# Revit family: Emeco_1inch_Reclaimed_Chair
name_source: partatom
category: Furniture
revit_build: Autodesk Revit 2016 (Build: 20150714_1515(x64)
units: mm (PartAtom-declared; Revit-internal decimal feet)

## family parameters
Always vertical = Yes
Cut with Voids When Loaded = No
OmniClass Number = 23.40.20.00
OmniClass Title = General Furniture and Specialties
Room Calculation Point = No
Shared = No
Work Plane-Based = No

## types (8) — shared parameters
1" Reclaimed Chair = Bordeaux
Depth = 1' - 8 29/32"
Height = 2' - 7 3/32"
Manufacturer = Emeco
Model = 1inch Reclaimed Chair
URL = https://www.emeco.net
Width = 1' - 8 19/32"

## per-type parameters (varying)
| type | Chair | Chair Material | Weight |
| 1inch Reclaimed Chair - Blue | Sand | Emeco-Wood_Polypropylene - Dark Grey | 11.5lb |
| 1inch Reclaimed Chair - Sand | Sand | Emeco-Wood_Polypropylene - Sand | 11.5lb |
| 1inch Reclaimed Chair - Light Grey | Light Grey | Emeco-Wood_Polypropylene - Light Grey | 11.5lb |
| 1inch Reclaimed Chair - Green | Green | Emeco-Wood_Polypropylene - Green | 11.5lb |
| 1inch Reclaimed Chair - Bordeaux | Bordeaux | Emeco-Wood_Polypropylene - Bordeaux | 11.5lb |
| 1inch Reclaimed Chair - Brown | Brown | Emeco-Wood_Polypropylene - Brown | 11.5lb |
| 1inch Reclaimed Chair - Orange | Orange | Emeco-Wood_Polypropylene - Orange | 11.5 lb |
| 1inch Reclaimed Chair - Dark Grey | Emeco-Wood_Polypropylene - Dark Grey | Emeco-Wood_Polypropylene - Dark Grey | 11.5lb |

## geometry (parser evidence)
native form markers: Sweep x3
no freeform markers — native parametric forms only
